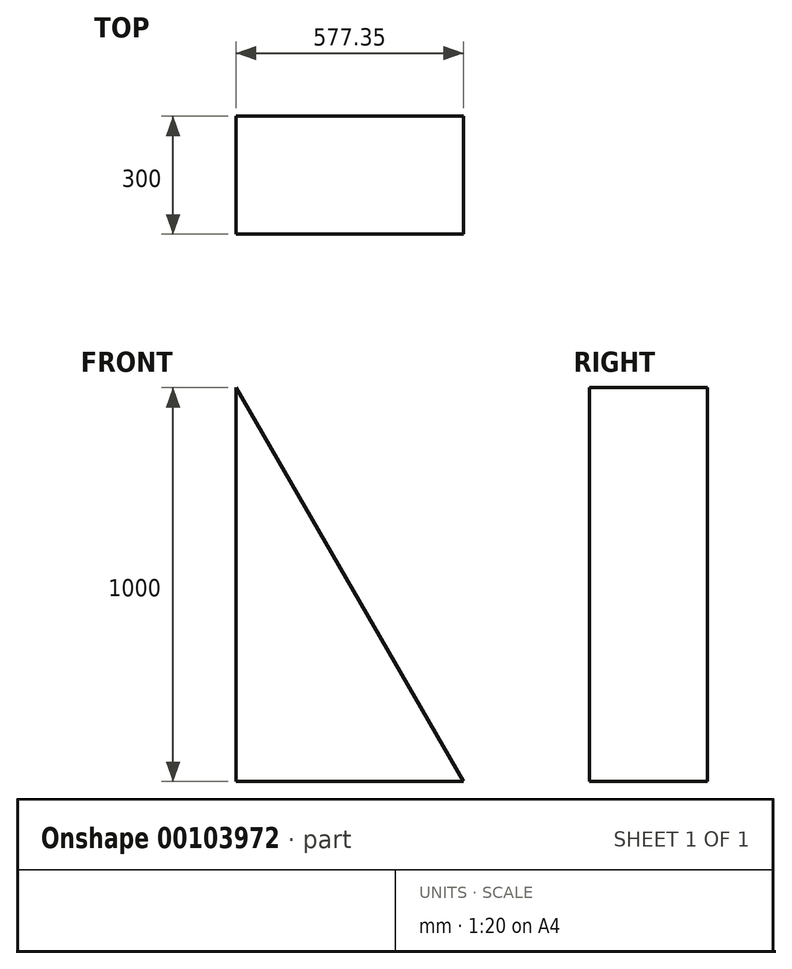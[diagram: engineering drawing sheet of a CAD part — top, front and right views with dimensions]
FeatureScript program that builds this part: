
annotation { "Feature Type Name" : "Feature", "Feature Type Description" : "" }
export const myFeature = defineFeature(function(context is Context, id is Id, definition is map)
    precondition{}
    {
        {
            var Q0;
            Q0=qCreatedBy(makeId("Front.planeOp"),FACE);
            var sketch = newSketch(context, id + "F0", { "sketchPlane" : qUnion([Q0])});
            skLineSegment(sketch, "E0", {"start": v(0, 0) * mm, "end": v(0, 1000) * mm});
            skLineSegment(sketch, "E1", {"start": v(0, 1000) * mm, "end": v(577.35, 0) * mm});
            skLineSegment(sketch, "E2", {"start": v(577.35, 0) * mm, "end": v(0, 0) * mm});
            skSolve(sketch);
        }
        {
            var Q0;
            Q0=makeQuery(id+"F0.imprint","IMPRINT",FACE,{"disambiguationData":[TD([[makeQuery(id+"F0.imprint","IMPRINT",EDGE,{"derivedFrom":sQuery(id+"F0.wireOp",EDGE,"E0")}),-1.0]])]});
            extrude(context, id + "F1", {"entities" : qUnion([Q0]), "endBound" : BoundingType.SYMMETRIC, "depth" : 300 * mm});
        }
    });
